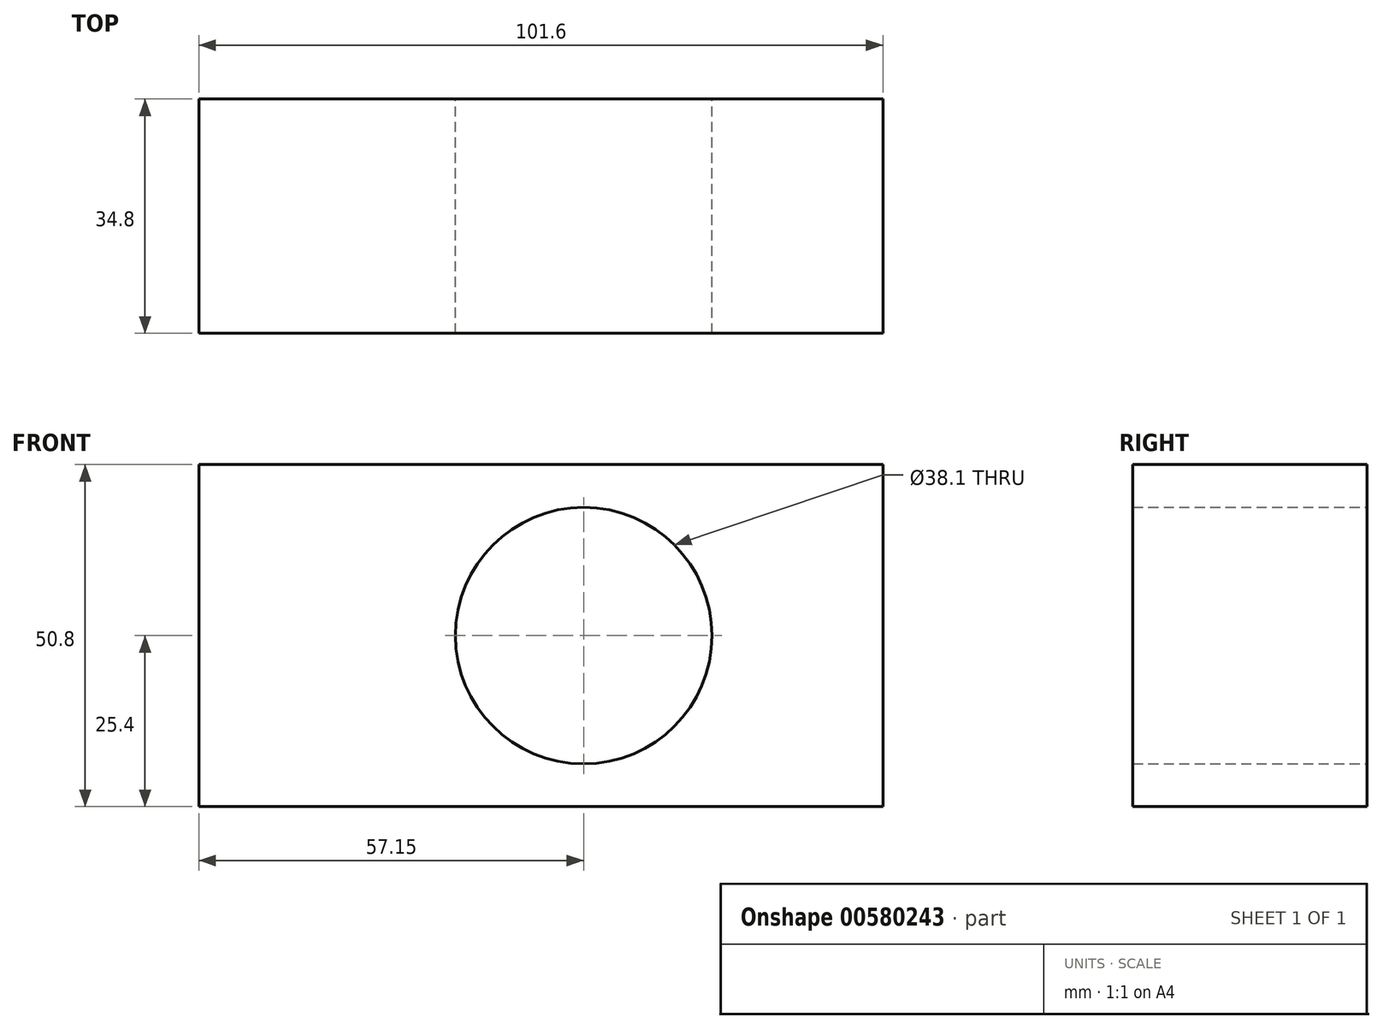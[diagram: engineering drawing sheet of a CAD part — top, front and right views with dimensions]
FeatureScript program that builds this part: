
annotation { "Feature Type Name" : "Feature", "Feature Type Description" : "" }
export const myFeature = defineFeature(function(context is Context, id is Id, definition is map)
    precondition{}
    {
        {
            var Q0;
            Q0=qCreatedBy(makeId("Front.planeOp"),FACE);
            var sketch = newSketch(context, id + "F0", { "sketchPlane" : qUnion([Q0])});
            skLineSegment(sketch, "E0.bottom", {"start": v(0, 0) * mm, "end": v(101.6, 0) * mm});
            skLineSegment(sketch, "E0.top", {"start": v(0, 50.8) * mm, "end": v(101.6, 50.8) * mm});
            skLineSegment(sketch, "E0.left", {"start": v(0, 0) * mm, "end": v(0, 50.8) * mm});
            skLineSegment(sketch, "E0.right", {"start": v(101.6, 0) * mm, "end": v(101.6, 50.8) * mm});
            skCircle(sketch, "E1", {"center": v(57.15, 25.4) * mm, "radius": 19.05 * mm});
            skSolve(sketch);
        }
        {
            var Q0;
            Q0 = qSketchRegion(id + "F0", true);
            extrude(context, id + "F1", {"entities" : qUnion([Q0]), "depth" : 34.8 * mm, "offsetDistance" : 25.4 * mm});
        }
    });
